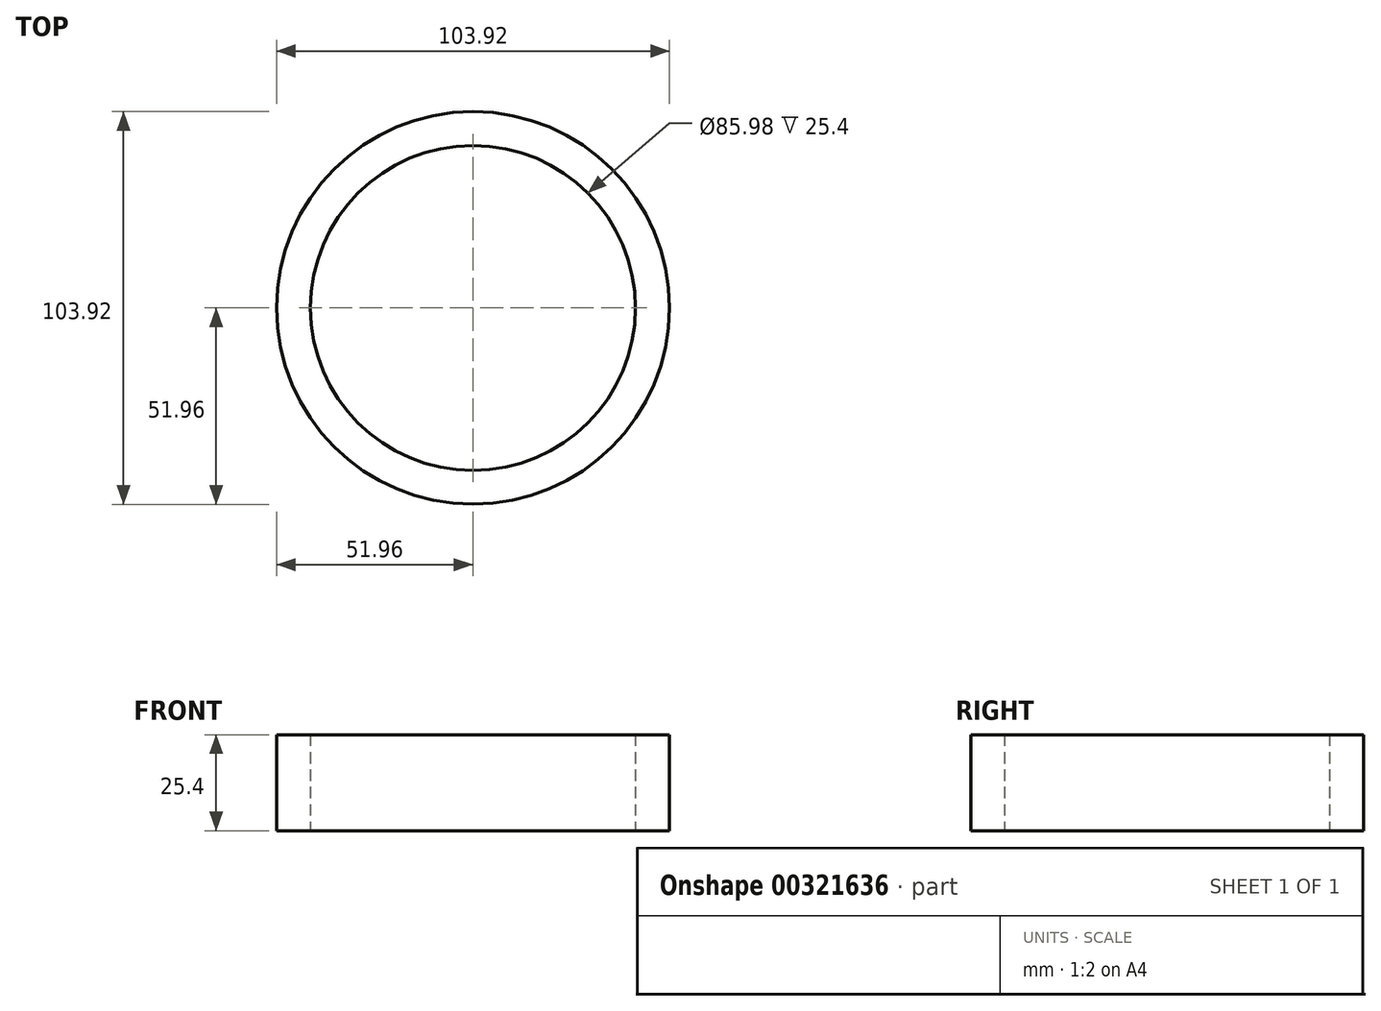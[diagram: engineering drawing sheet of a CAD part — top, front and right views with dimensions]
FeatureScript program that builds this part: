
annotation { "Feature Type Name" : "Feature", "Feature Type Description" : "" }
export const myFeature = defineFeature(function(context is Context, id is Id, definition is map)
    precondition{}
    {
        {
            var Q0;
            Q0=qCreatedBy(makeId("Top.planeOp"),FACE);
            var sketch = newSketch(context, id + "F0", { "sketchPlane" : qUnion([Q0])});
            skCircle(sketch, "E0", {"center": v(0, 0) * mm, "radius": 51.96 * mm});
            skCircle(sketch, "E1", {"center": v(0, 0) * mm, "radius": 42.99 * mm});
            skSolve(sketch);
        }
        {
            var Q0;
            Q0 = qSketchRegion(id + "F0", true);
            extrude(context, id + "F1", {"entities" : qUnion([Q0]), "depth" : 25.4 * mm});
        }
    });
